# Revit family: Faucet_Touchless-Lavatory-KOHLER-Accliv-K-32942T
name_source: partatom
category: Plumbing Fixtures
units: mm (PartAtom-declared; Revit-internal decimal feet)

## family parameters
Cut with Voids When Loaded = No
Host = Face
OmniClass Number = 23.31.11.00
OmniClass Title = Faucets
Part Type = Normal
Room Calculation Point = No
Round Connector Dimension = Use Diameter
Shared = No

## types (4) — shared parameters
ADA Compliant = No
Assembly Code = D2010
CW Connection = Yes
Cold Water Inlet = Cold Water Inlet
Date Modified = 03/15/2024
Default Elevation = 36"
Description = Single Handle Tall Touchless Faucet
Drain Included = Yes
HW Connection = Yes
Handle Clearance = 4 1/16"
Height = 9 7/16"
Hot Water Inlet = Hot Water Inlet
Length = 5 13/16"
Manufacturer = Kohler Co.
Master Format 2014 = 22 41 39
Master Format 2014 Name = Residential Faucets, Supplies, and Trim
Material = Premium Metal Construction
Pressure = 60.00 psi
Product Name = Accliv
Spout Reach = 5 13/16"
URL = http://www.kohler.com.cn
Vent Connection = No
Waste Connection = No
Waste Water Outlet = Waste Water Outlet
WaterSense Certified = No
Width = 2"

## per-type parameters (varying)
| type | Finish | Flow Rate | Model | Secondary Finish | Type |
| 2.2 GPM, BL-Matte Black | Kohler-Metal-BL-Matte_Black | 2 GPM | K-32942T-4-BL | Silicone-Pantone-Black_C | 1 |
| 2.2 GPM, CP-Polished Chrome | Kohler-Metal-CP-Polished_Chrome | 2 GPM | K-32942T-4-CP | Plastic-Pantone-425C | 2 |
| 1.2 GPM, BL-Matte Black | Kohler-Metal-BL-Matte_Black | 1 GPM | K-32942T-4E2-BL | Silicone-Pantone-Black_C | 3 |
| 1.2 GPM, CP-Polished Chrome | Kohler-Metal-CP-Polished_Chrome | 1 GPM | K-32942T-4E2-CP | Plastic-Pantone-425C | 4 |

## geometry (parser evidence)
native form markers: Sweep x5
no freeform markers — native parametric forms only
